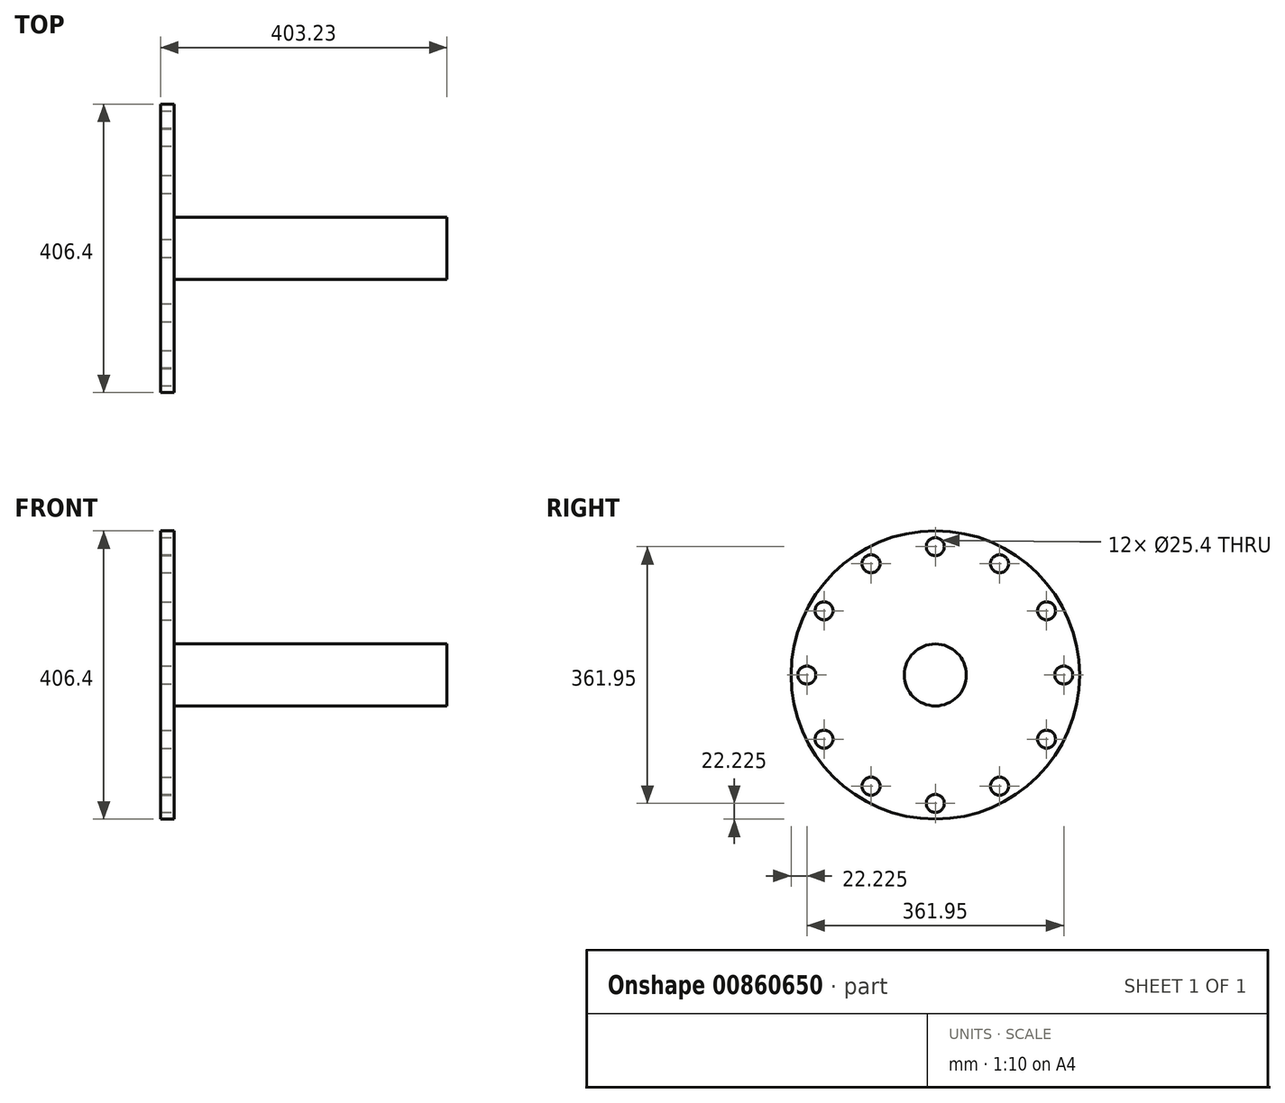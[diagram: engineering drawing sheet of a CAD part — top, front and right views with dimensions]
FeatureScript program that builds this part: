
annotation { "Feature Type Name" : "Feature", "Feature Type Description" : "" }
export const myFeature = defineFeature(function(context is Context, id is Id, definition is map)
    precondition{}
    {
        {
            var Q0;
            Q0=qCreatedBy(makeId("Front.planeOp"),FACE);
            var sketch = newSketch(context, id + "F0", { "sketchPlane" : qUnion([Q0])});
            skLineSegment(sketch, "E0", {"start": v(0, 0) * mm, "end": v(0, 203.2) * mm});
            skLineSegment(sketch, "E1", {"start": v(0, 203.2) * mm, "end": v(19.05, 203.2) * mm});
            skLineSegment(sketch, "E2", {"start": v(19.05, 203.2) * mm, "end": v(19.05, 43.66) * mm});
            skLineSegment(sketch, "E3", {"start": v(19.05, 43.66) * mm, "end": v(403.23, 43.66) * mm});
            skLineSegment(sketch, "E4", {"start": v(403.23, 43.66) * mm, "end": v(403.23, 0) * mm});
            skLineSegment(sketch, "E5", {"start": v(403.23, 0) * mm, "end": v(0, 0) * mm});
            skSolve(sketch);
        }
        {
            var Q0;
            Q0=makeQuery(id+"F0.imprint","IMPRINT",FACE,{"disambiguationData":[TD([[makeQuery(id+"F0.imprint","IMPRINT",EDGE,{"derivedFrom":sQuery(id+"F0.wireOp",EDGE,"E0")}),-1.0]])]});
            var Q1;
            Q1=sQuery(id+"F0.wireOp",EDGE,"E5");
            revolve(context, id + "F1", {"surfaceOperationType" : NewSurfaceOperationType.NEW, "entities" : qUnion([Q0]), "axis" : qUnion([Q1]), "revolveType" : RevolveType.FULL});
        }
        {
            var Q0;
            Q0=makeQuery(id+"F1.opRevolve","SWEPT_FACE",FACE,{"disambiguationData":[OSD([sQuery(id+"F0.wireOp",EDGE,"E2")])]});
            var sketch = newSketch(context, id + "F2", { "sketchPlane" : qUnion([Q0])});
            skLineSegment(sketch, "E6", {"start": v(0, 0) * mm, "end": v(0, 180.98) * mm});
            skPoint(sketch, "E7", {"position": v(0, 180.98) * mm});
            skPoint(sketch, "E8.1.0", {"position": v(-90.49, 156.73) * mm});
            skPoint(sketch, "E8.2.0", {"position": v(-156.73, 90.49) * mm});
            skPoint(sketch, "E8.3.0", {"position": v(-180.98, 0) * mm});
            skPoint(sketch, "E8.4.0", {"position": v(-156.73, -90.49) * mm});
            skPoint(sketch, "E8.5.0", {"position": v(-90.49, -156.73) * mm});
            skPoint(sketch, "E8.6.0", {"position": v(0, -180.98) * mm});
            skPoint(sketch, "E8.7.0", {"position": v(90.49, -156.73) * mm});
            skPoint(sketch, "E8.8.0", {"position": v(156.73, -90.49) * mm});
            skPoint(sketch, "E8.9.0", {"position": v(180.98, 0) * mm});
            skPoint(sketch, "E8.10.0", {"position": v(156.73, 90.49) * mm});
            skPoint(sketch, "E8.11.0", {"position": v(90.49, 156.73) * mm});
            skPoint(sketch, "E8.center", {"position": v(0, 0) * mm});
            skSolve(sketch);
        }
        {
            var Q0;
            Q0=sQuery(id+"F2.wireOp",VERTEX,"E7");
            var Q1;
            Q1=sQuery(id+"F2.wireOp",VERTEX,"E8.11.0");
            var Q2;
            Q2=sQuery(id+"F2.wireOp",VERTEX,"E8.10.0");
            var Q3;
            Q3=sQuery(id+"F2.wireOp",VERTEX,"E8.9.0");
            var Q4;
            Q4=sQuery(id+"F2.wireOp",VERTEX,"E8.8.0");
            var Q5;
            Q5=sQuery(id+"F2.wireOp",VERTEX,"E8.7.0");
            var Q6;
            Q6=sQuery(id+"F2.wireOp",VERTEX,"E8.6.0");
            var Q7;
            Q7=sQuery(id+"F2.wireOp",VERTEX,"E8.5.0");
            var Q8;
            Q8=sQuery(id+"F2.wireOp",VERTEX,"E8.4.0");
            var Q9;
            Q9=sQuery(id+"F2.wireOp",VERTEX,"E8.3.0");
            var Q10;
            Q10=sQuery(id+"F2.wireOp",VERTEX,"E8.2.0");
            var Q11;
            Q11=sQuery(id+"F2.wireOp",VERTEX,"E8.1.0");
            var Q12;
            Q12=makeQuery(id+"F1.opRevolve","SWEPT_BODY",BODY,{"disambiguationData":[OSD([sQuery(id+"F0.wireOp",EDGE,"E0"),sQuery(id+"F0.wireOp",EDGE,"E1"),sQuery(id+"F0.wireOp",EDGE,"E2"),sQuery(id+"F0.wireOp",EDGE,"E3"),sQuery(id+"F0.wireOp",EDGE,"E4"),sQuery(id+"F0.wireOp",EDGE,"E5")])]});
            hole(context, id + "F3", {"style" : HoleStyle.SIMPLE, "endStyle" : HoleEndStyle.THROUGH, "holeDiameter" : 25.4 * mm, "majorDiameter" : 6.35 * mm, "isTappedThrough" : true, "tappedDepth" : 12.7 * mm, "tapClearance" : 3, "locations" : qUnion([Q0, Q1, Q2, Q3, Q4, Q5, Q6, Q7, Q8, Q9, Q10, Q11]), "scope" : qUnion([Q12])});
        }
    });
